# Revit family: York CB-ABM-YK - Active Modular Chilled Beam, Face Base, Revit 2015 R1.0
name_source: partatom
category: Mechanical Equipment
revit_build: Autodesk Revit 2015 (Build: 20160512_1515(x64)
units: mm (PartAtom-declared; Revit-internal decimal feet)

## types (5) — shared parameters
(0) Front and Back Supply = Yes
(1) Front Supply = No
(2) Back Supply = No
0 - No Insulation = Yes
26 - White = Yes
2P1C - 2 Pipe Coils = No
3 - Lay-In = Yes
4" Dia. = No
4P1C - 4 Pipe Coils = Yes
5" Dia. = No
6" Dia./6" Oval = Yes
8" Dia. = No
84 - Black Paint = No
Arrow Length = 6"
B1 = Yes
B2 = No
B3 = No
B4 = No
BL - Linear bar grille = No
CP - Circular Perforation = Yes
CTR Clearnce Material = Clearance
CTR Inlet Pipe Dia = 1/4"
CTR Left Right Connection = No
CTR Pipe System = 3 1/8"
CTR Pipe Y Dist = 2 5/8"
CTR R3 Connector Ellipse Height = 3 3/16"
CTR R4 Connector Width = 6 1/2"
CTR R5 Connector Ellipse Width = 6 1/2"
CTR Side Inlet Connection = No
Chilled Water Connection Diameter = 1"
D1 (Top Inlet) = 5 7/8"
D2 = 5 5/8"
DF - Tegular 15/16 = No
Default Elevation = 48"
Description = Active Modular Chilled Beam • 4-Way Discharge • Horizontal Coil
Finish Color = 1
Frame Height = 7"
H12 - SS flex hose - 12in = No
H18 - SS flex hose - 18in = No
H24 - SS flex hose - 24in = No
Heating Water Connection Diameter = 1"
Inlet pipe Angle = 0.00°
L - 1/2 Ecoshield (Foil face) = No
MPT - Male Pipe Thread = No
Manufacturer = York
Material = Casing is extruded Aluminum and galvanealed G90.
Model = CB-ABM-YK
Mounting Bracket Visible = Yes
NT - Tegular 9/16 = No
Neck Size = 10"
Nominal Inlet Dia Connector = 6"
Nominal Inlet Dia Oval Connector H = 5 1/4"
Nominal Inlet Dia Oval Connector W = 6 1/2"
Oval Height Minus R2 = 2 1/2"
Oval Height R2 = 2 5/8"
Ovel Width = 2"
Pipe Location Left Side = Yes
Pipe Location Right Side = No
R1 (Left Right Side) = 3 1/4"
R2 Minus = 3 1/8"
SWT - Sweat = Yes
Select a Border Type = 1
Select a Nominal Air Inlet Dia. = 3
Select a Water-Coil Type = 2
Select the Air Nozzle Configuration = 1
Select the Grille's Air Pattern Face = 2
Select the Piping Connection Type = 1
Select the Plenum Liner (External) = 1
Support Distance = 24 3/8"
URL = http://www.york.com
Width = 23 3/4"
zero-valued in all types: Water Connection Location Selection

## per-type parameters (varying)
| type | A | Angle | B | Bracket Distance | Bracket Length | CTR Left Right Box Visible | CTR Left Right oval Connection Visible | CTR Perforated Plate L | CTR Side Inlet Oval Connection | CTR Top Inlet Connection | Length | Pipe Rotate length | Select a Module Size and Air Inlet location | Version |
| 24x24 Top Inlet | 11 7/8" | 180.00° | 5 1/8" | 2" | 6" | No | No | 17 1/8" | No | Yes | 23 3/4" | 7 11/16" | 1 | 2 |
| 48x24 Top Inlet | 11 7/8" | 180.00° | 5 1/8" | 5" | 12" | No | No | 41 1/8" | No | Yes | 47 3/4" | 19 177/256" | 2 | 0 |
| 24x24 Side Inlet | 11 7/8" | 180.00° | 5 1/8" | 2" | 6" | No | No | 17 1/8" | Yes | No | 23 3/4" | 7 11/16" | 3 | 0 |
| 48x24 Left Side Inlet | 5 1/8" | 0.00° | 11 7/8" | 5" | 12" | Yes | Yes | 41 1/8" | No | No | 47 3/4" | 19 177/256" | 4 | 0 |
| 48x24 Right Side Inlet | 11 7/8" | 180.00° | 5 1/8" | 5" | 12" | Yes | Yes | 41 1/8" | No | No | 47 3/4" | 19 177/256" | 5 | 0 |

type visibility flags: 5 boolean params named "<type name>" — each type sets only its own to Yes (folded from table)

## geometry (parser evidence)
native form markers: Blend x2, Sweep x11
no freeform markers — native parametric forms only
